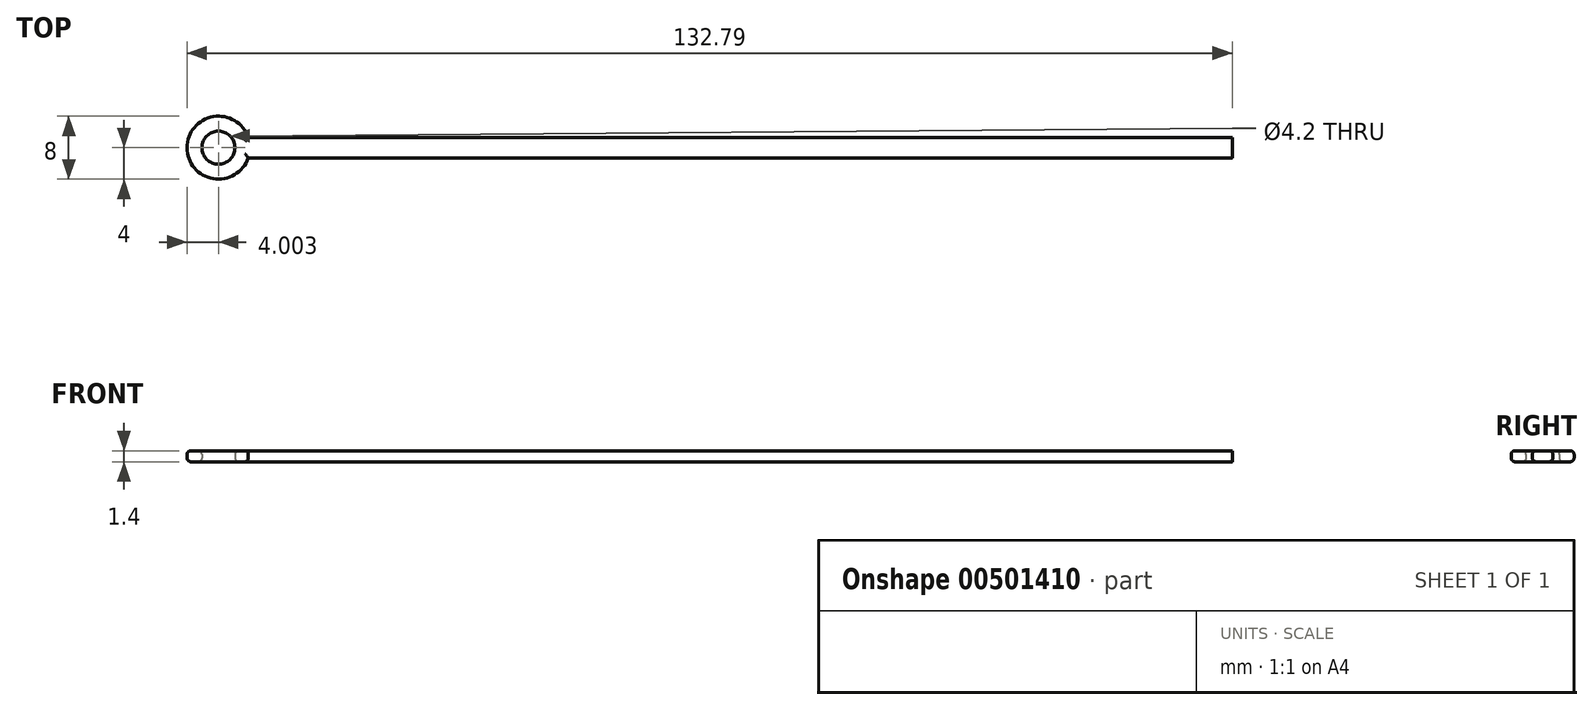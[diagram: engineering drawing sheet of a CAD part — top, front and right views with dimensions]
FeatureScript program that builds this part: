
annotation { "Feature Type Name" : "Feature", "Feature Type Description" : "" }
export const myFeature = defineFeature(function(context is Context, id is Id, definition is map)
    precondition{}
    {
        {
            var Q0;
            Q0=qCreatedBy(makeId("Top.planeOp"),FACE);
            var sketch = newSketch(context, id + "F0", { "sketchPlane" : qUnion([Q0])});
            skLineSegment(sketch, "E0", {"start": v(-124.47, 0) * mm, "end": v(125.84, 0) * mm, "construction": true});
            skLineSegment(sketch, "E1", {"start": v(-115.83, 8.87) * mm, "end": v(-115.83, -11.15) * mm, "construction": true});
            skCircle(sketch, "E2", {"center": v(-115.83, 0) * mm, "radius": 2.1 * mm});
            skCircle(sketch, "E3", {"center": v(-115.83, 0) * mm, "radius": 4 * mm});
            skLineSegment(sketch, "E4", {"start": v(-112.04, 1.3) * mm, "end": v(12.96, 1.3) * mm});
            skLineSegment(sketch, "E5", {"start": v(12.96, 1.3) * mm, "end": v(12.96, 0) * mm});
            skLineSegment(sketch, "E6.MirrorCS", {"start": v(-112.04, -1.3) * mm, "end": v(12.96, -1.3) * mm});
            skLineSegment(sketch, "E7", {"start": v(12.96, 0) * mm, "end": v(12.96, -1.3) * mm});
            skSolve(sketch);
        }
        {
            var Q0;
            Q0=makeQuery(id+"F0.imprint","IMPRINT",FACE,{"disambiguationData":[TD([[makeQuery(id+"F0.imprint","IMPRINT",EDGE,{"derivedFrom":sQuery(id+"F0.wireOp",EDGE,"E2")}),-1.0]])]});
            extrude(context, id + "F1", {"entities" : qUnion([Q0]), "endBound" : BoundingType.SYMMETRIC, "depth" : 1.4 * mm, "offsetDistance" : 25 * mm});
        }
        {
            var Q0;
            {var subQ1=sQuery(id+"F0.wireOp",EDGE,"E4");Q0=makeQuery(id+"F0.imprint","IMPRINT",FACE,{"disambiguationData":[TD([[makeQuery(id+"F0.imprint","IMPRINT",EDGE,{"derivedFrom":subQ1}),-1.0]])]});}
            extrude(context, id + "F2", {"entities" : qUnion([Q0]), "operationType" : NewBodyOperationType.ADD, "endBound" : BoundingType.SYMMETRIC, "depth" : 1.4 * mm, "offsetDistance" : 25 * mm});
        }
        {
            var Q0;
            Q0=makeQuery(id+"F1.opExtrude","CAP_EDGE",EDGE,{"disambiguationData":[OSD([sQuery(id+"F0.wireOp",EDGE,"E2")])],"isStart":false});
            var Q1;
            Q1=makeQuery(id+"F1.opExtrude","CAP_EDGE",EDGE,{"disambiguationData":[OSD([sQuery(id+"F0.wireOp",EDGE,"E2")])],"isStart":true});
            var Q2;
            Q2=makeQuery(id+"F1.opExtrude","CAP_EDGE",EDGE,{"disambiguationData":[OSD([sQuery(id+"F0.wireOp",EDGE,"E3")])],"isStart":true});
            var Q3;
            Q3=makeQuery(id+"F1.opExtrude","CAP_EDGE",EDGE,{"disambiguationData":[OSD([sQuery(id+"F0.wireOp",EDGE,"E3")])],"isStart":false});
            var Q4;
            Q4=makeQuery(id+"F2.opExtrude","CAP_EDGE",EDGE,{"disambiguationData":[OSD([sQuery(id+"F0.wireOp",EDGE,"E4")])],"isStart":false});
            var Q5;
            Q5=makeQuery(id+"F2.opExtrude","CAP_EDGE",EDGE,{"disambiguationData":[OSD([sQuery(id+"F0.wireOp",EDGE,"E6.MirrorCS")])],"isStart":false});
            var Q6;
            Q6=makeQuery(id+"F2.opExtrude","CAP_EDGE",EDGE,{"disambiguationData":[OSD([sQuery(id+"F0.wireOp",EDGE,"E4")])],"isStart":true});
            var Q7;
            Q7=makeQuery(id+"F2.opExtrude","CAP_EDGE",EDGE,{"disambiguationData":[OSD([sQuery(id+"F0.wireOp",EDGE,"E6.MirrorCS")])],"isStart":true});
            fillet(context, id + "F3", {"entities" : qUnion([Q0, Q1, Q2, Q3, Q4, Q5, Q6, Q7]), "radius" : .5 * mm, "tangentPropagation" : true, "allowEdgeOverflow" : false});
        }
    });
